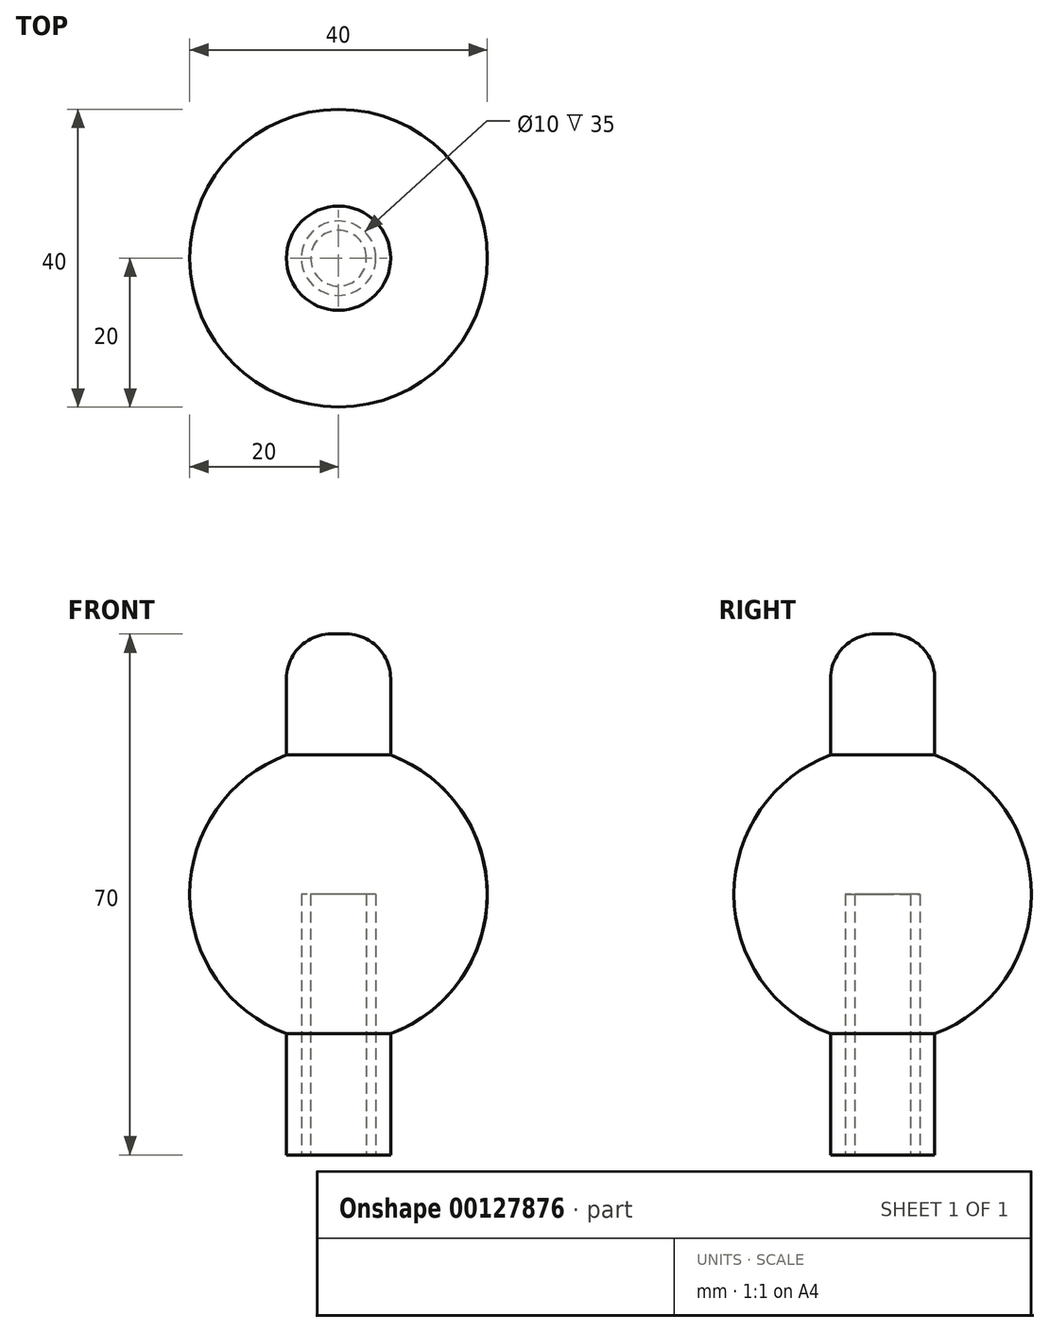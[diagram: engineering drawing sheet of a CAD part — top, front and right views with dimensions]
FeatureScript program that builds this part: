
annotation { "Feature Type Name" : "Feature", "Feature Type Description" : "" }
export const myFeature = defineFeature(function(context is Context, id is Id, definition is map)
    precondition{}
    {
        {
            var Q0;
            Q0=qCreatedBy(makeId("Top.planeOp"),FACE);
            var sketch = newSketch(context, id + "F0", { "sketchPlane" : qUnion([Q0])});
            skCircle(sketch, "E0", {"center": v(0, 0) * mm, "radius": 3.75 * mm});
            skCircle(sketch, "E1", {"center": v(0, 0) * mm, "radius": 5 * mm});
            skCircle(sketch, "E2", {"center": v(0, 0) * mm, "radius": 7 * mm});
            skSolve(sketch);
        }
        {
            var Q0;
            Q0=makeQuery(id+"F0.imprint","IMPRINT",FACE,{"disambiguationData":[TD([[makeQuery(id+"F0.imprint","IMPRINT",EDGE,{"derivedFrom":sQuery(id+"F0.wireOp",EDGE,"E0")}),1.0]])]});
            var Q1;
            Q1=makeQuery(id+"F0.imprint","IMPRINT",FACE,{"disambiguationData":[TD([[makeQuery(id+"F0.imprint","IMPRINT",EDGE,{"derivedFrom":sQuery(id+"F0.wireOp",EDGE,"E1")}),-1.0]])]});
            var Q2;
            Q2=makeQuery(id+"F0.imprint","IMPRINT",FACE,{"disambiguationData":[TD([[makeQuery(id+"F0.imprint","IMPRINT",EDGE,{"derivedFrom":sQuery(id+"F0.wireOp",EDGE,"E0")}),-1.0]])]});
            extrude(context, id + "F1", {"entities" : qUnion([Q0, Q1, Q2]), "depth" : 70 * mm});
        }
        {
            var Q0;
            Q0=qCreatedBy(makeId("Front.planeOp"),FACE);
            var sketch = newSketch(context, id + "F2", { "sketchPlane" : qUnion([Q0])});
            skLineSegment(sketch, "E3", {"start": v(0, 15) * mm, "end": v(0, 55) * mm});
            skArc(sketch, "E4", {"start": v(0, 55) * mm, "mid": v(-20, 35) * mm, "end": v(0, 15) * mm});
            skSolve(sketch);
        }
        {
            var Q0;
            Q0=makeQuery(id+"F2.imprint","IMPRINT",FACE,{"disambiguationData":[TD([[makeQuery(id+"F2.imprint","IMPRINT",EDGE,{"derivedFrom":sQuery(id+"F2.wireOp",EDGE,"E3")}),1.0]])]});
            var Q1;
            Q1=sQuery(id+"F2.wireOp",EDGE,"E3");
            revolve(context, id + "F3", {"operationType" : NewBodyOperationType.ADD, "entities" : qUnion([Q0]), "axis" : qUnion([Q1]), "revolveType" : RevolveType.FULL});
        }
        {
            var Q0;
            Q0=makeQuery(id+"F0.imprint","IMPRINT",FACE,{"disambiguationData":[TD([[makeQuery(id+"F0.imprint","IMPRINT",EDGE,{"derivedFrom":sQuery(id+"F0.wireOp",EDGE,"E0")}),-1.0]])]});
            extrude(context, id + "F4", {"entities" : qUnion([Q0]), "operationType" : NewBodyOperationType.REMOVE, "depth" : 35 * mm});
        }
        {
            var Q0;
            Q0=makeQuery(id+"F1.opExtrude","CAP_EDGE",EDGE,{"disambiguationData":[OSD([sQuery(id+"F0.wireOp",EDGE,"E2")])],"isStart":false});
            fillet(context, id + "F5", {"entities" : qUnion([Q0]), "radius" : 6 * mm, "tangentPropagation" : true, "allowEdgeOverflow" : false});
        }
    });
